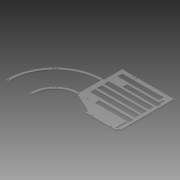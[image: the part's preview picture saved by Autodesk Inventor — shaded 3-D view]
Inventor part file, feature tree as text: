
AUTODESK INVENTOR PART (.ipt)
format: ipt  version: 2013 (Build 170138000, 138)  size: 518,656 bytes
history: native  units: in
note: dims shown in document units (in); Inventor stores cm internally (conversion verified against a paired STEP export)
features: extrude x16, sketch x16, reference x2
ambient origin geometry x8: Origin, YZ Plane, XZ Plane, XY Plane, X Axis, Y Axis, Z Axis, Center Point
feature tree (34):
  extrude  "Extrusion7"  Depth=1.0in
  extrude  "Extrusion8"  Depth=0.5in
  extrude  "Extrusion9"  Depth=5.25in
  extrude  "Extrusion10"  Depth=0.25in
  extrude  "Extrusion11"  Depth=7.625in
  extrude  "Extrusion13"  Depth=5.5in
  extrude  "Extrusion15"  Depth=12.125in
  extrude  "Extrusion16"  Depth=8.0in
  extrude  "Extrusion17"  Depth=2.75in
  extrude  "Extrusion18"  TaperAngle=90.0deg  [1 undecoded]
  extrude  "Extrusion19"  Depth=0.75in
  extrude  "Extrusion20"  Depth=10.5in
  extrude  "Extrusion21"  Depth=0.75in
  extrude  "Extrusion22"  Depth=10.5in
  extrude  "Extrusion23"  Depth=1.125in
  extrude  "Extrusion24"  Depth=0.5in
  sketch  "Sketch1"  dims[d2=0.5in d3=0.5in d10=0.5in d11=0.5in d13=0.5in d14=0.266in d15=0.266in d16=0.266in d18=0.266in d20=0.25in d21=0.266in d22=0.266in d23=0.266in d26=0.266in d30=0.266in d32=0.266in d66=1.0in]
  sketch  "Sketch7"  dims[d67=0.0in d72=0.5in]
  sketch  "Sketch8"  dims[d81=4.25in d82=5.25in]
  sketch  "Sketch9"  dims[d83=11.0in d84=0.25in]
  sketch  "Sketch10"  dims[d85=12.5in d86=7.625in]
  sketch  "Sketch13"  dims[d87=2.1762in d88=5.5in]
  sketch  "Sketch14"  dims[d89=0.25in d90=0.0in d91=12.125in]
  reference  "Reference4"
  sketch  "Sketch16"  dims[d92=1.0in d93=8.0in]
  sketch  "Sketch17"  dims[d94=0.5in d95=2.75in]
  sketch  "Sketch18"  dims[d98=0.25in d99=0.0in d100=90.0deg]
  sketch  "Sketch19"  dims[d101=0.875in d102=0.75in]
  sketch  "Sketch20"  dims[d103=1.125in d104=10.5in]
  reference  "Reference9"
  sketch  "Sketch21"  dims[d105=1.125in d106=0.75in]
  sketch  "Sketch22"  dims[d107=0.5in d108=10.5in]
  sketch  "Sketch23"  dims[d109=1.125in d110=1.125in]
  sketch  "Sketch24"  dims[d111=0.5in d112=0.5in d113=10.5in d114=0.75in d115=0.75in d116=1.0in d117=0.0in d118=11.125in d119=0.25in d120=11.5in d121=1.0in d122=0.0in d123=0.5in d124=1.375in d125=135.0deg d126=0.25in d127=0.0in d135=1.0in d136=13.25in d137=0.5in d138=1.0in d139=0.0in d146=0.25in d148=0.25in d149=0.375in d150=1.0in d151=0.0in d153=0.25in d154=0.0in d155=0.5in d156=0.5in d157=0.25in d158=0.0in d159=1.25in d160=0.25in d161=0.0in d162=0.266in d164=0.25in d165=2.75in d166=1.0in d167=0.0in d168=1.0in d169=0.0in d170=0.266in d171=0.266in d172=1.125in d173=1.375in d174=1.125in d176=0.125in d177=1.0in d178=0.0in d179=0.875in d180=0.25in d181=0.0in d182=0.875in d183=0.25in d184=0.0in d185=0.25in d186=0.0in]
note: 1 required parameter value undecoded (feature->parameter linkage not recoverable at this tier; creation-order binding heuristic only, values carry confidence <= 0.55)
